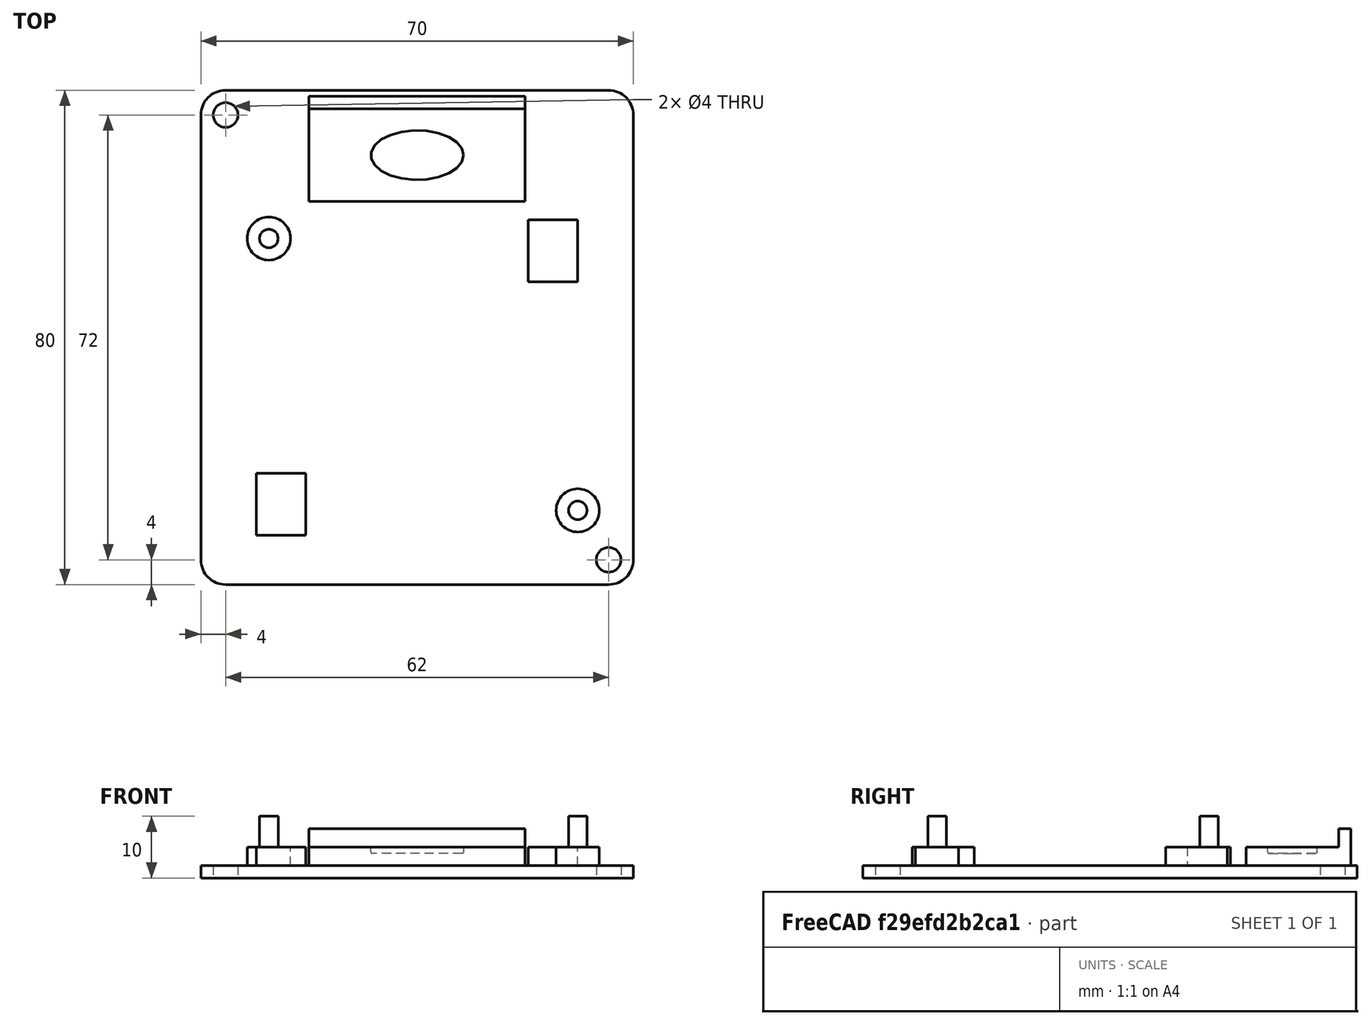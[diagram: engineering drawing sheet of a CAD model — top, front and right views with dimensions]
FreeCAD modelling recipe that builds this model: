
FCSTD DOCUMENT  (FreeCAD 0.21R33771 (Git))
Label: BasePlate_rev1
License: All rights reserved
LicenseURL: http://en.wikipedia.org/wiki/All_rights_reserved
objects: Sketcher::SketchObject×7, PartDesign::Pad×7, PartDesign::Fillet×2, PartDesign::Pocket×1, PartDesign::Hole×1, PartDesign::Body×1, TechDraw::DrawSVGTemplate×1, TechDraw::DrawViewPart×1, TechDraw::DrawViewBalloon×1, TechDraw::DrawPage×1
note: 30 computed .brp shape members not serialized (recipe doc carries the construction recipe); baked Part::Feature solids carry a one-line shape summary decoded from their .brp

FEATURE [Sketcher::SketchObject] Sketch
  FullyConstrained = true
  MapMode = 5
  Support = -> [XY_Plane]
  sketch-geometry (4):
    g0: LineSegment StartX=0 StartY=0 StartZ=0 EndX=70 EndY=0 EndZ=0
    g1: LineSegment StartX=70 StartY=0 StartZ=0 EndX=70 EndY=80 EndZ=0
    g2: LineSegment StartX=70 StartY=80 StartZ=0 EndX=0 EndY=80 EndZ=0
    g3: LineSegment StartX=0 StartY=80 StartZ=0 EndX=0 EndY=0 EndZ=0
  constraints (11):
    c: Coincident(g0,g1)
    c: Coincident(g1,g2)
    c: Coincident(g2,g3)
    c: Coincident(g3,g0)
    c: Horizontal(g0)
    c: Horizontal(g2)
    c: Vertical(g1)
    c: Vertical(g3)
    c: Coincident(g0,g-1)
    c: DistanceX(g0,g0) = 70
    c: DistanceY(g1,g1) = 80
FEATURE [PartDesign::Pad] Pad
  Direction = (0,0,1)
  Length = 2
  Length2 = 10
  Profile = -> Sketch
  ReferenceAxis = -> Sketch [N_Axis]
  Type = 0
FEATURE [Sketcher::SketchObject] Sketch001
  ExternalGeometry = -> [Pad]
  FullyConstrained = true
  MapMode = 5
  Placement = pos=(0,0,2) rot=(0,0,1;0rad)
  Support = -> [Pad]
  sketch-geometry (8):
    g0: LineSegment StartX=4 StartY=8 StartZ=0 EndX=66 EndY=8 EndZ=0
    g1: LineSegment StartX=66 StartY=8 StartZ=0 EndX=66 EndY=59 EndZ=0
    g2: LineSegment StartX=66 StartY=59 StartZ=0 EndX=4 EndY=59 EndZ=0
    g3: LineSegment StartX=4 StartY=59 StartZ=0 EndX=4 EndY=8 EndZ=0
    g4: GeomPoint X=35 Y=8 Z=0
    g5: GeomPoint X=35 Y=0 Z=0
    g6: Circle CenterX=11 CenterY=56 CenterZ=0 NormalX=0 NormalY=0 NormalZ=1 AngleXU=0 Radius=3.5
    g7: Circle CenterX=61 CenterY=12 CenterZ=0 NormalX=0 NormalY=0 NormalZ=1 AngleXU=0 Radius=3.5
  constraints (20):
    c: Coincident(g0,g1)
    c: Coincident(g1,g2)
    c: Coincident(g2,g3)
    c: Coincident(g3,g0)
    c: Horizontal(g0)
    c: Horizontal(g2)
    c: Vertical(g1)
    c: Vertical(g3)
    c: DistanceX(g0,g0) = 62
    c: DistanceY(g1,g1) = 51
    c: Symmetric(g0,g0,g4)
    c: Symmetric(g-4,g-5,g5)
    c: Vertical(g4,g5)
    c: DistanceY(g-4,g0) = 8
    c: DistanceX(g2,g6) = 7
    c: DistanceX(g7,g0) = 5
    c: DistanceY(g6,g2) = 3
    c: DistanceY(g0,g7) = 4
    c: Diameter(g6) = 7
    c: Diameter(g7) = 7
FEATURE [PartDesign::Pad] Pad001
  BaseFeature = -> Pad
  Direction = (0,0,1)
  Length = 3
  Length2 = 10
  Profile = -> Sketch001
  ReferenceAxis = -> Sketch001 [N_Axis]
  Type = 0
FEATURE [Sketcher::SketchObject] Sketch002
  ExternalGeometry = -> [Pad001]
  FullyConstrained = true
  MapMode = 5
  Placement = pos=(0,0,5) rot=(0,0,1;0rad)
  Support = -> [Pad001]
  sketch-geometry (2):
    g0: Circle CenterX=11 CenterY=56 CenterZ=0 NormalX=0 NormalY=0 NormalZ=1 AngleXU=0 Radius=1.5
    g1: Circle CenterX=61 CenterY=12 CenterZ=0 NormalX=0 NormalY=0 NormalZ=1 AngleXU=0 Radius=1.5
  constraints (4):
    c: Coincident(g0,g-3)
    c: Coincident(g1,g-4)
    c: Diameter(g0) = 3
    c: Equal(g1,g0)
FEATURE [PartDesign::Pad] Pad002
  BaseFeature = -> Pad001
  Direction = (0,0,1)
  Length = 5
  Length2 = 10
  Profile = -> Sketch002
  ReferenceAxis = -> Sketch002 [N_Axis]
  Type = 0
FEATURE [Sketcher::SketchObject] Sketch003
  ExternalGeometry = -> [Pad002]
  FullyConstrained = true
  MapMode = 5
  Placement = pos=(0,0,2) rot=(0,0,1;0rad)
  Support = -> [Pad002]
  sketch-geometry (6):
    g0: LineSegment StartX=17.5 StartY=77 StartZ=0 EndX=52.5 EndY=77 EndZ=0
    g1: LineSegment StartX=52.5 StartY=77 StartZ=0 EndX=52.5 EndY=62 EndZ=0
    g2: LineSegment StartX=52.5 StartY=62 StartZ=0 EndX=17.5 EndY=62 EndZ=0
    g3: LineSegment StartX=17.5 StartY=62 StartZ=0 EndX=17.5 EndY=77 EndZ=0
    g4: GeomPoint X=35 Y=77 Z=0
    g5: GeomPoint X=35 Y=80 Z=0
  constraints (14):
    c: Coincident(g0,g1)
    c: Coincident(g1,g2)
    c: Coincident(g2,g3)
    c: Coincident(g3,g0)
    c: Horizontal(g0)
    c: Horizontal(g2)
    c: Vertical(g1)
    c: Vertical(g3)
    c: DistanceY(g1,g1) = 15
    c: DistanceX(g2,g2) = 35
    c: Symmetric(g0,g0,g4)
    c: Symmetric(g-3,g-3,g5)
    c: Vertical(g5,g4)
    c: DistanceY(g4,g5) = 3
FEATURE [PartDesign::Pad] Pad003
  BaseFeature = -> Pad002
  Direction = (0,0,1)
  Length = 3
  Length2 = 10
  Profile = -> Sketch003
  ReferenceAxis = -> Sketch003 [N_Axis]
  Type = 0
FEATURE [PartDesign::Pad] Pad004
  BaseFeature = -> Pad003
  Direction = (0,1,0)
  Length = 2
  Length2 = 10
  Profile = -> Pad003 [Face12]
  Type = 0
FEATURE [PartDesign::Pad] Pad005
  BaseFeature = -> Pad004
  Direction = (0,0,1)
  Length = 3
  Length2 = 10
  Profile = -> Pad004 [Face18]
  Type = 0
FEATURE [Sketcher::SketchObject] Sketch004
  ExternalGeometry = -> [Pad005]
  FullyConstrained = true
  MapMode = 5
  Placement = pos=(0,0,5) rot=(0,0,1;0rad)
  Support = -> [Pad005]
  sketch-geometry (7):
    g0: Ellipse CenterX=35 CenterY=69.5 CenterZ=0 NormalX=0 NormalY=0 NormalZ=1 MajorRadius=7.5 MinorRadius=4 AngleXU=0
    g1: LineSegment StartX=42.5 StartY=69.5 StartZ=0 EndX=27.5 EndY=69.5 EndZ=0
    g2: LineSegment StartX=35 StartY=73.5 StartZ=0 EndX=35 EndY=65.5 EndZ=0
    g3: GeomPoint X=41.3443 Y=69.5 Z=0
    g4: GeomPoint X=28.6557 Y=69.5 Z=0
    g5: GeomPoint X=35 Y=69.5 Z=0
    g6: GeomPoint X=52.5 Y=69.5 Z=0
  constraints (7):
    c: InternalAlignment(g1-g4 -> g0) x4
    c: Symmetric(g-4,g-3,g5)
    c: Coincident(g0,g5)
    c: DistanceX(g1,g1) = 15
    c: DistanceY(g2,g2) = 8
    c: Symmetric(g-3,g-3,g6)
    c: Horizontal(g3,g6)
FEATURE [PartDesign::Pocket] Pocket
  BaseFeature = -> Pad005
  Direction = (0,0,-1)
  Length = 1
  Length2 = 5
  Profile = -> Sketch004
  ReferenceAxis = -> Sketch004 [N_Axis]
  Type = 0
FEATURE [PartDesign::Fillet] Fillet
  Base = -> Pocket [Edge54]
  BaseFeature = -> Pocket
  Radius = 0.2
  SupportTransform = false
  UseAllEdges = false
FEATURE [PartDesign::Fillet] Fillet001
  Base = -> Fillet [Edge39,Edge40,Edge44,Edge42]
  BaseFeature = -> Fillet
  Radius = 4
  SupportTransform = false
  UseAllEdges = false
FEATURE [Sketcher::SketchObject] Sketch005
  ExternalGeometry = -> [Fillet001]
  FullyConstrained = true
  MapMode = 5
  Placement = pos=(0,0,2) rot=(0,0,1;0rad)
  Support = -> [Fillet001]
  sketch-geometry (2):
    g0: Circle CenterX=4 CenterY=76 CenterZ=0 NormalX=0 NormalY=0 NormalZ=1 AngleXU=0 Radius=1.5
    g1: Circle CenterX=66 CenterY=4 CenterZ=0 NormalX=0 NormalY=0 NormalZ=1 AngleXU=0 Radius=1.5
  constraints (4):
    c: Coincident(g-4,g0)
    c: Coincident(g1,g-3)
    c: Diameter(g1) = 3
    c: Diameter(g0) = 3
FEATURE [PartDesign::Hole] Hole
  BaseFeature = -> Fillet001
  CustomThreadClearance = 0
  Depth = 25
  DepthType = 0
  Diameter = 4
  DrillForDepth = false
  DrillPoint = 1
  DrillPointAngle = 118
  HoleCutCountersinkAngle = 90
  HoleCutCustomValues = false
  HoleCutDepth = 0
  HoleCutDiameter = 6.1
  HoleCutType = 0
  ModelThread = false
  Profile = -> Sketch005
  Tapered = false
  TaperedAngle = 90
  ThreadClass = 0
  ThreadDepth = 25
  ThreadDepthType = 0
  ThreadDirection = 0
  ThreadFit = 0
  ThreadSize = 0
  ThreadType = 0
  Threaded = false
  UseCustomThreadClearance = false
FEATURE [Sketcher::SketchObject] Sketch006
  ExternalGeometry = -> [Pad]
  FullyConstrained = true
  MapMode = 5
  Placement = pos=(0,0,2) rot=(0,0,1;0rad)
  Support = -> [Hole]
  expr: Constraints[13] = Sketch001.Constraints[13]
  expr: Constraints[8] = Sketch001.Constraints[8]
  expr: Constraints[9] = Sketch001.Constraints[9]
  sketch-geometry (14):
    g0: LineSegment StartX=4 StartY=8 StartZ=0 EndX=66 EndY=8 EndZ=0
    g1: LineSegment StartX=66 StartY=8 StartZ=0 EndX=66 EndY=59 EndZ=0
    g2: LineSegment StartX=66 StartY=59 StartZ=0 EndX=4 EndY=59 EndZ=0
    g3: LineSegment StartX=4 StartY=59 StartZ=0 EndX=4 EndY=8 EndZ=0
    g4: GeomPoint X=35 Y=8 Z=0
    g5: GeomPoint X=35 Y=0 Z=0
    g6: LineSegment StartX=61 StartY=59 StartZ=0 EndX=53 EndY=59 EndZ=0
    g7: LineSegment StartX=53 StartY=59 StartZ=0 EndX=53 EndY=49 EndZ=0
    g8: LineSegment StartX=53 StartY=49 StartZ=0 EndX=61 EndY=49 EndZ=0
    g9: LineSegment StartX=61 StartY=49 StartZ=0 EndX=61 EndY=59 EndZ=0
    g10: LineSegment StartX=9 StartY=8 StartZ=0 EndX=17 EndY=8 EndZ=0
    g11: LineSegment StartX=17 StartY=8 StartZ=0 EndX=17 EndY=18 EndZ=0
    g12: LineSegment StartX=17 StartY=18 StartZ=0 EndX=9 EndY=18 EndZ=0
    g13: LineSegment StartX=9 StartY=18 StartZ=0 EndX=9 EndY=8 EndZ=0
  constraints (38):
    c: Coincident(g0,g1)
    c: Coincident(g1,g2)
    c: Coincident(g2,g3)
    c: Coincident(g3,g0)
    c: Horizontal(g0)
    c: Horizontal(g2)
    c: Vertical(g1)
    c: Vertical(g3)
    c: DistanceX(g0,g0) = 62
    c: DistanceY(g1,g1) = 51
    c: Symmetric(g0,g0,g4)
    c: Symmetric(g-4,g-5,g5)
    c: Vertical(g4,g5)
    c: DistanceY(g-4,g0) = 8
    c: Coincident(g6,g7)
    c: Coincident(g7,g8)
    c: Coincident(g8,g9)
    c: Coincident(g9,g6)
    c: Horizontal(g6)
    c: Horizontal(g8)
    c: Vertical(g7)
    c: Vertical(g9)
    c: PointOnObject(g6,g2)
    c: Coincident(g10,g11)
    c: Coincident(g11,g12)
    c: Coincident(g12,g13)
    c: Coincident(g13,g10)
    c: Horizontal(g10)
    c: Horizontal(g12)
    c: Vertical(g11)
    c: Vertical(g13)
    c: PointOnObject(g10,g0)
    c: DistanceX(g12,g12) = 8
    c: Equal(g12,g8)
    c: DistanceY(g11,g11) = 10
    c: Equal(g11,g9)
    c: DistanceX(g0,g10) = 5
    c: DistanceX(g6,g1) = 5
FEATURE [PartDesign::Pad] Pad006
  BaseFeature = -> Hole
  Direction = (0,0,1)
  Length = 10
  Length2 = 10
  Profile = -> Sketch006
  ReferenceAxis = -> Sketch006 [N_Axis]
  Type = 3
  UpToFace = -> Hole [Face22]
FEATURE [PartDesign::Body] Body
  Group = -> [Sketch,Pad,Sketch001,Pad001,Sketch002,Pad002,Sketch003,Pad003,Pad004,Pad005,Sketch004,Pocket,Fillet,Fillet001,Sketch005,Hole,Sketch006,Pad006]
  Origin = -> Origin
  Tip = -> Pad006
FEATURE [TechDraw::DrawSVGTemplate] Template
  Height = 297
  Orientation = 0
  Template = <path>
  Width = 210
FEATURE [TechDraw::DrawViewPart] View  label="ESP32-GATEWAY mount"
  CoarseView = false
  Direction = (0.57639,-0.571542,0.58405)
  Focus = 100
  HardHidden = false
  IsoCount = 0
  IsoHidden = false
  IsoVisible = false
  LockPosition = false
  Perspective = false
  Rotation = 0
  ScaleType = 0
  ScrubCount = 0
  SeamHidden = false
  SeamVisible = false
  SmoothHidden = false
  SmoothVisible = true
  Source = -> [Body]
  X = 95.4
  XDirection = (0.737116,0.672165,-0.0696792)
  Y = 245.947
FEATURE [TechDraw::DrawViewBalloon] Balloon
  BubbleShape = 1
  EndType = 0
  EndTypeScale = 1
  KinkLength = 5
  LockPosition = false
  OriginX = 30.6151
  OriginY = 14.4909
  Rotation = 0
  ScaleType = 0
  ShapeScale = 1
  SourceView = -> View
  Text = RS485-Board mount
  TextWrapLen = -1
  X = 71.3045
  Y = 23.0873
FEATURE [TechDraw::DrawPage] Page
  KeepUpdated = true
  NextBalloonIndex = 2
  ProjectionType = 0
  Template = -> Template
  Views = -> [View,Balloon]
note: 1 file-system path scrubbed to <path> (originals preserved in the JSON sidecar)
